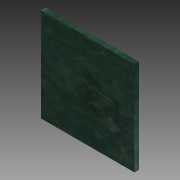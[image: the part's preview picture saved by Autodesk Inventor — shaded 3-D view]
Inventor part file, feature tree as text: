
AUTODESK INVENTOR PART (.ipt)
format: ipt  version: 2013 (Build 170138000, 138)  size: 99,328 bytes
history: native  units: in
note: dims shown in document units (in); Inventor stores cm internally (conversion verified against a paired STEP export)
features: plane x2, extrude x1, other x1, sketch x1
ambient origin geometry x8: Origin, YZ Plane, XZ Plane, XY Plane, X Axis, Y Axis, Z Axis, Center Point
bodies: Solid1 (feature_tree)
feature tree (5):
  extrude  "Extrusion1"  Depth=5.0in
  other  "Work Axis1"
  sketch  "Sketch1"  dims[d0=5.0in d1=5.0in d2=0.25in d3=0.0in]
  plane  "Work Plane1"
  plane  "Work Plane2"
